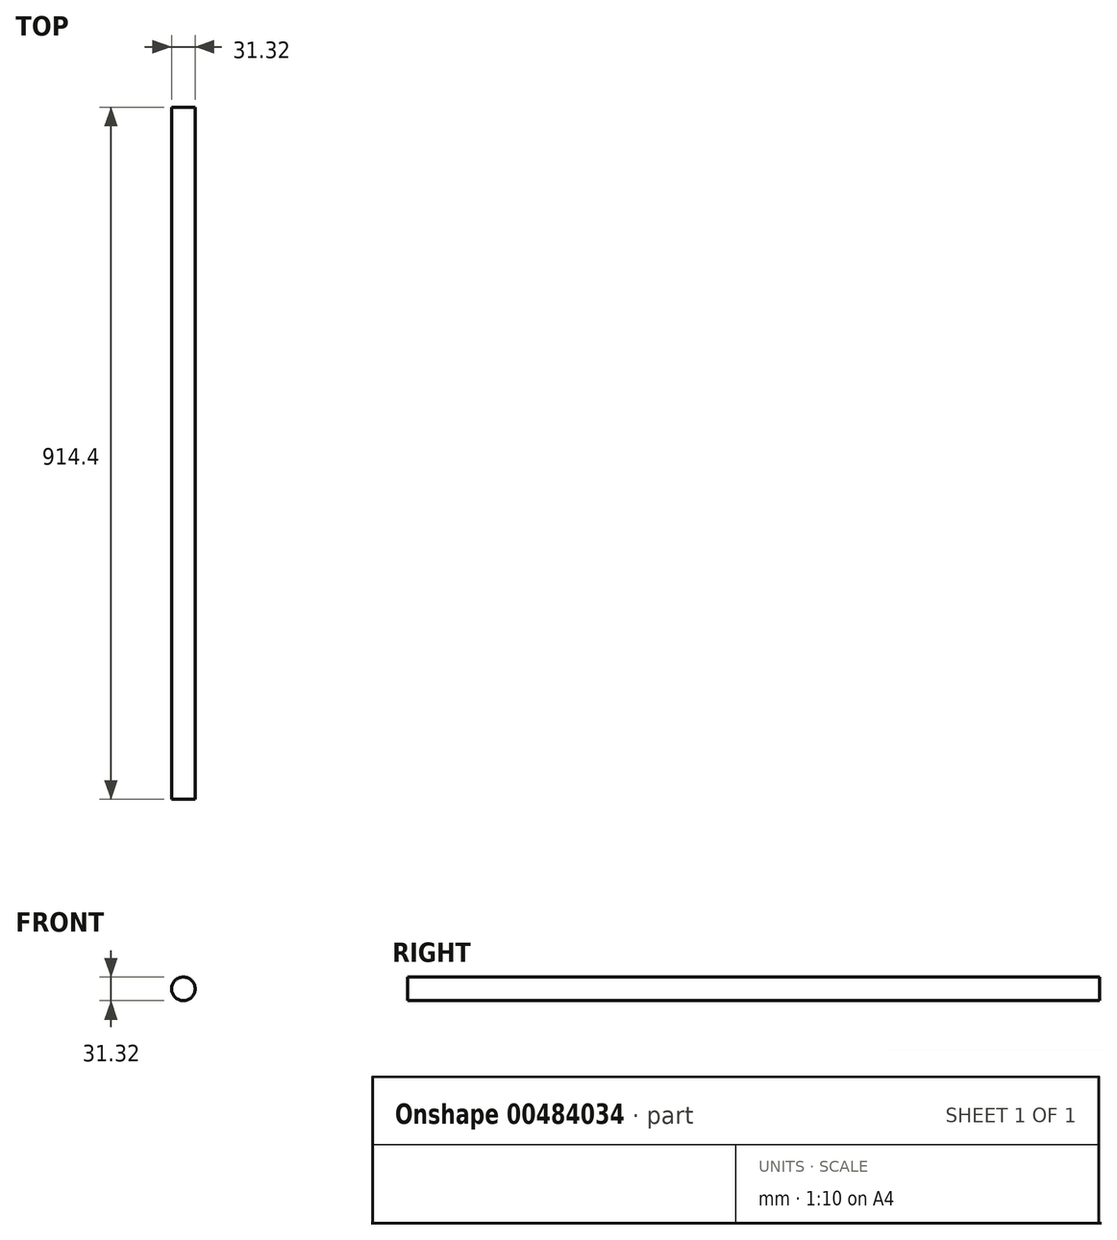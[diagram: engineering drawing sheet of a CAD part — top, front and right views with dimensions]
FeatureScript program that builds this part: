
annotation { "Feature Type Name" : "Feature", "Feature Type Description" : "" }
export const myFeature = defineFeature(function(context is Context, id is Id, definition is map)
    precondition{}
    {
        {
            var Q0;
            Q0=qCreatedBy(makeId("Front.planeOp"),FACE);
            var sketch = newSketch(context, id + "F0", { "sketchPlane" : qUnion([Q0])});
            skCircle(sketch, "E0", {"center": v(0, 0) * mm, "radius": 15.66 * mm});
            skSolve(sketch);
        }
        {
            var Q0;
            Q0 = qSketchRegion(id + "F0", true);
            extrude(context, id + "F1", {"entities" : qUnion([Q0]), "depth" : 914.4 * mm});
        }
    });
